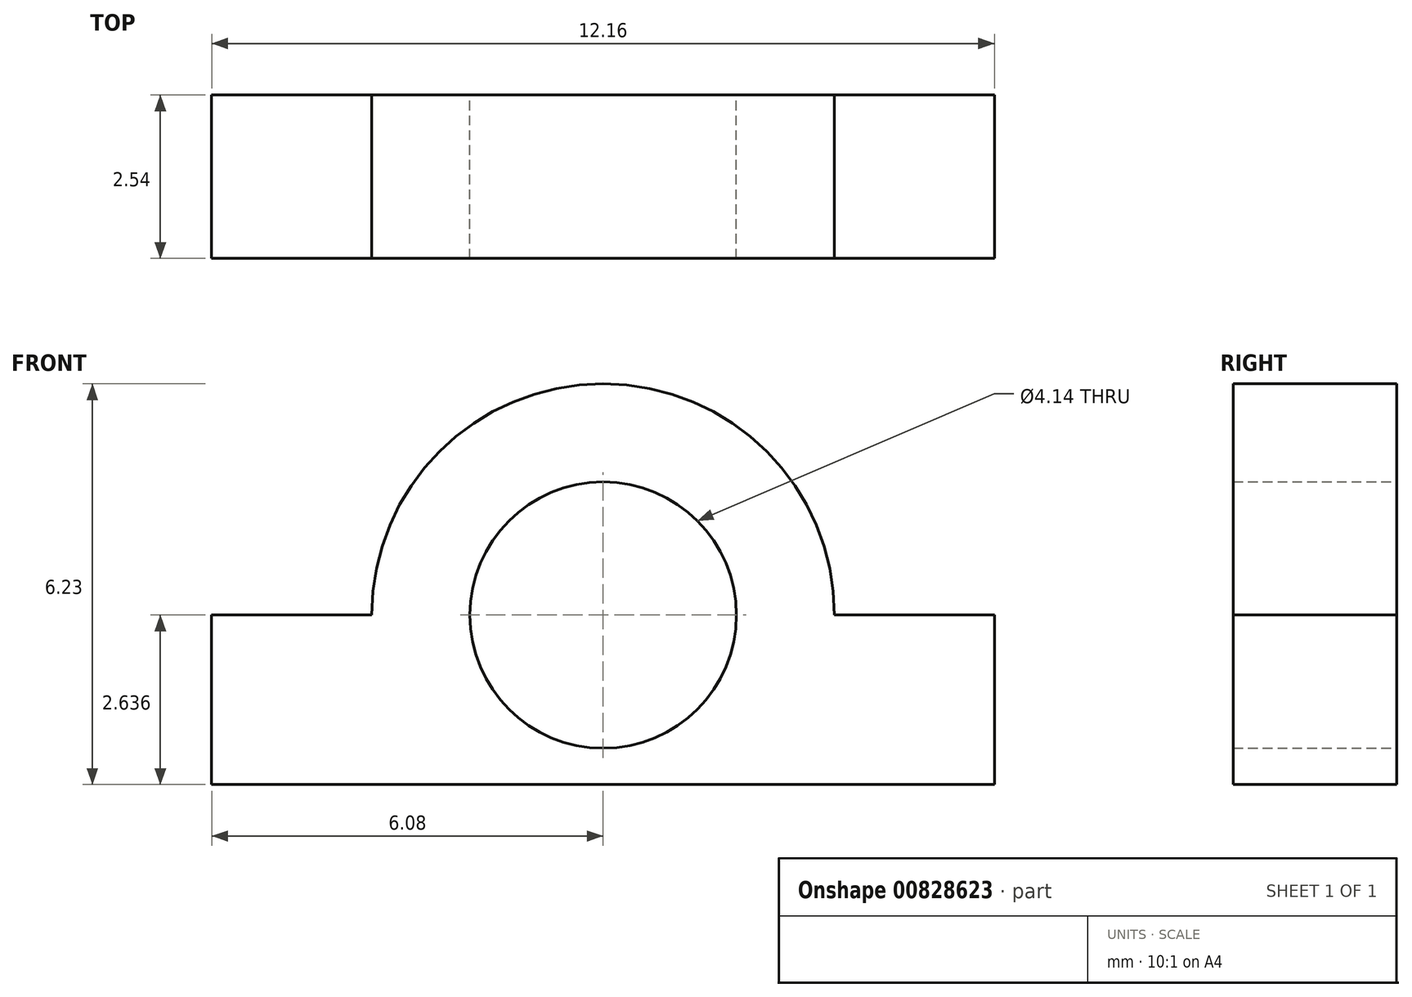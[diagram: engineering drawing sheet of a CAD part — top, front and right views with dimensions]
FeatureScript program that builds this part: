
annotation { "Feature Type Name" : "Feature", "Feature Type Description" : "" }
export const myFeature = defineFeature(function(context is Context, id is Id, definition is map)
    precondition{}
    {
        {
            var Q0;
            Q0=qCreatedBy(makeId("Front.planeOp"),FACE);
            var sketch = newSketch(context, id + "F0", { "sketchPlane" : qUnion([Q0])});
            skLineSegment(sketch, "E0.bottom", {"start": v(6.08, 1.32) * mm, "end": v(-6.08, 1.32) * mm});
            skLineSegment(sketch, "E0.top", {"start": v(6.08, -1.32) * mm, "end": v(-6.08, -1.32) * mm});
            skLineSegment(sketch, "E0.left", {"start": v(6.08, 1.32) * mm, "end": v(6.08, -1.32) * mm});
            skLineSegment(sketch, "E0.right", {"start": v(-6.08, 1.32) * mm, "end": v(-6.08, -1.32) * mm});
            skPoint(sketch, "E0.middle", {"position": v(0, 0) * mm});
            skArc(sketch, "E1", {"start": v(2.45, -1.32) * mm, "mid": v(0, 4.91) * mm, "end": v(-2.45, -1.32) * mm});
            skCircle(sketch, "E2", {"center": v(0, 1.32) * mm, "radius": 2.07 * mm});
            skSolve(sketch);
        }
        {
            var Q0;
            Q0 = qSketchRegion(id + "F0", true);
            extrude(context, id + "F1", {"entities" : qUnion([Q0]), "depth" : 2.54 * mm, "offsetDistance" : 25.4 * mm});
        }
    });
